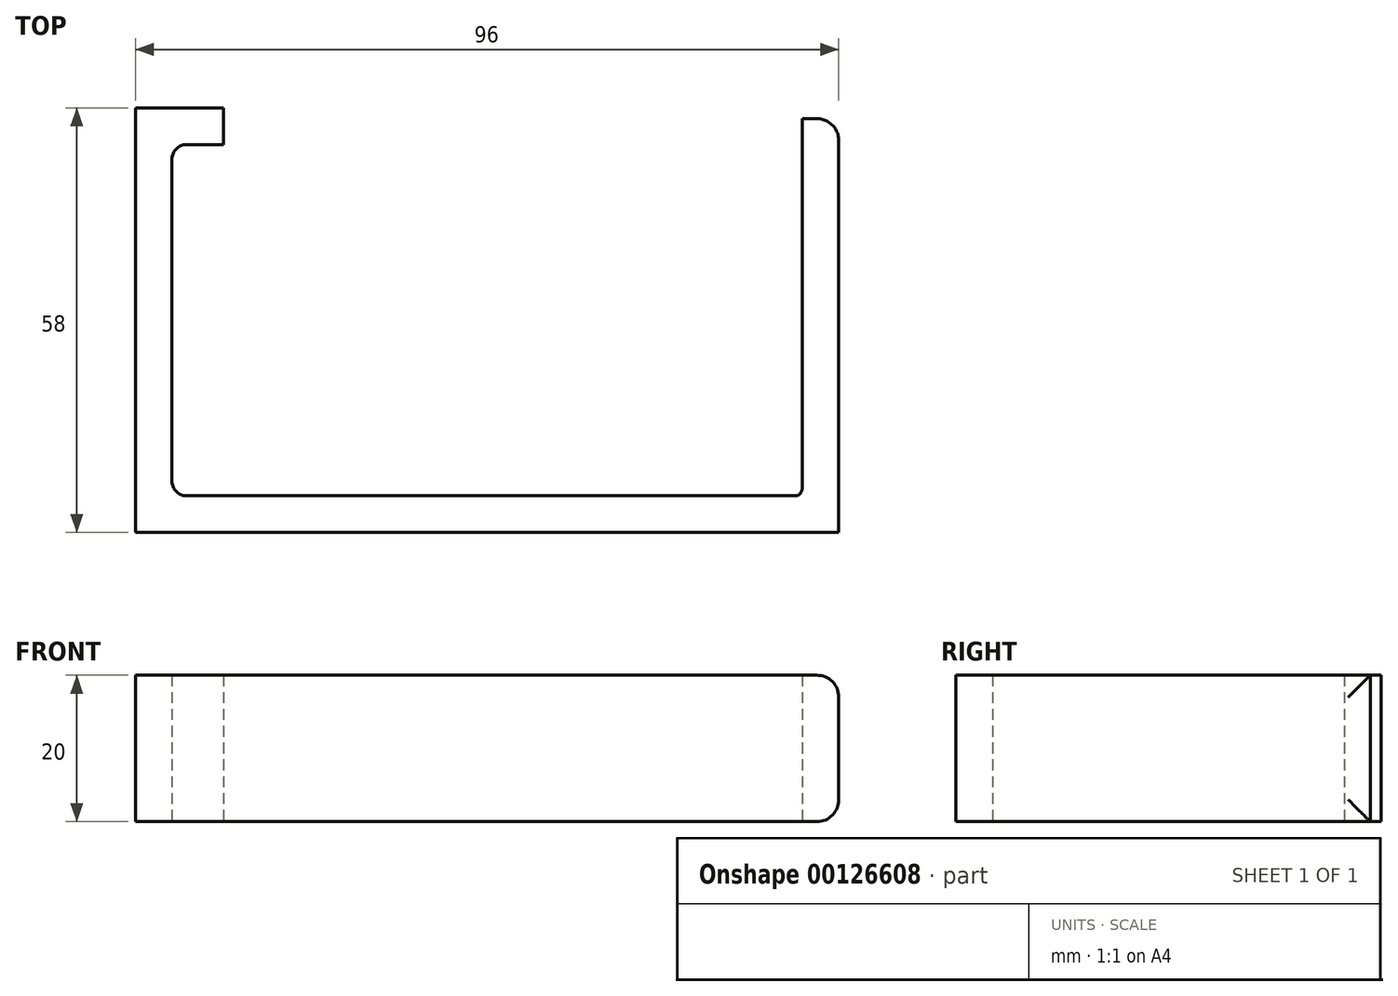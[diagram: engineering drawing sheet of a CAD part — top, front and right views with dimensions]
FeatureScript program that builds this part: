
annotation { "Feature Type Name" : "Feature", "Feature Type Description" : "" }
export const myFeature = defineFeature(function(context is Context, id is Id, definition is map)
    precondition{}
    {
        {
            var Q0;
            Q0=qCreatedBy(makeId("Top.planeOp"),FACE);
            var sketch = newSketch(context, id + "F0", { "sketchPlane" : qUnion([Q0])});
            skLineSegment(sketch, "E0", {"start": v(0, 0) * mm, "end": v(-86, 0) * mm});
            skLineSegment(sketch, "E1", {"start": v(-86, 0) * mm, "end": v(-86, 48) * mm});
            skLineSegment(sketch, "E2", {"start": v(-86, 48) * mm, "end": v(-79, 48) * mm});
            skLineSegment(sketch, "E3.0", {"start": v(-91, 53) * mm, "end": v(-79, 53) * mm});
            skLineSegment(sketch, "E3.1", {"start": v(-91, -5) * mm, "end": v(-91, 53) * mm});
            skLineSegment(sketch, "E3.2", {"start": v(0, -5) * mm, "end": v(-91, -5) * mm});
            skLineSegment(sketch, "E4", {"start": v(-79, 53) * mm, "end": v(-79, 48) * mm});
            skLineSegment(sketch, "E5", {"start": v(0, -5) * mm, "end": v(0, 0) * mm});
            skLineSegment(sketch, "E6", {"start": v(0, 0) * mm, "end": v(0, 51.53) * mm});
            skLineSegment(sketch, "E7.0", {"start": v(5, 0) * mm, "end": v(5, 51.53) * mm});
            skLineSegment(sketch, "E7.1", {"start": v(5, -5) * mm, "end": v(5, 0) * mm});
            skLineSegment(sketch, "E8", {"start": v(5, -5) * mm, "end": v(0, -5) * mm});
            skLineSegment(sketch, "E9", {"start": v(5, 51.53) * mm, "end": v(0, 51.53) * mm});
            skSolve(sketch);
        }
        {
            var Q0;
            Q0 = qSketchRegion(id + "F0", true);
            extrude(context, id + "F1", {"entities" : qUnion([Q0]), "depth" : 20 * mm});
        }
        {
            var Q0;
            Q0=makeQuery(id+"F1.opExtrude","SWEPT_EDGE",EDGE,{"disambiguationData":[OSD([sQuery(id+"F0.wireOp",EDGE,"E0"),sQuery(id+"F0.wireOp",EDGE,"E5"),sQuery(id+"F0.wireOp",EDGE,"E6")])]});
            fillet(context, id + "F2", {"entities" : qUnion([Q0]), "radius" : 1 * mm, "tangentPropagation" : true, "allowEdgeOverflow" : false});
        }
        {
            var Q0;
            Q0=makeQuery(id+"F1.opExtrude","SWEPT_EDGE",EDGE,{"disambiguationData":[OSD([sQuery(id+"F0.wireOp",EDGE,"E1"),sQuery(id+"F0.wireOp",EDGE,"E2")])]});
            var Q1;
            Q1=makeQuery(id+"F1.opExtrude","SWEPT_EDGE",EDGE,{"disambiguationData":[OSD([sQuery(id+"F0.wireOp",EDGE,"E0"),sQuery(id+"F0.wireOp",EDGE,"E1")])]});
            fillet(context, id + "F3", {"entities" : qUnion([Q0, Q1]), "radius" : 2 * mm, "tangentPropagation" : true, "allowEdgeOverflow" : false});
        }
        {
            var Q0;
            Q0=makeQuery(id+"F1.opExtrude","CAP_EDGE",EDGE,{"disambiguationData":[OSD([sQuery(id+"F0.wireOp",EDGE,"E7.0"),sQuery(id+"F0.wireOp",EDGE,"E7.1")])],"isStart":true});
            var Q1;
            Q1=makeQuery(id+"F1.opExtrude","SWEPT_EDGE",EDGE,{"disambiguationData":[OSD([sQuery(id+"F0.wireOp",EDGE,"E7.0"),sQuery(id+"F0.wireOp",EDGE,"E9")])]});
            var Q2;
            Q2=makeQuery(id+"F1.opExtrude","CAP_EDGE",EDGE,{"disambiguationData":[OSD([sQuery(id+"F0.wireOp",EDGE,"E7.0"),sQuery(id+"F0.wireOp",EDGE,"E7.1")])],"isStart":false});
            fillet(context, id + "F4", {"entities" : qUnion([Q0, Q1, Q2]), "radius" : 3 * mm, "tangentPropagation" : true, "allowEdgeOverflow" : false});
        }
    });
